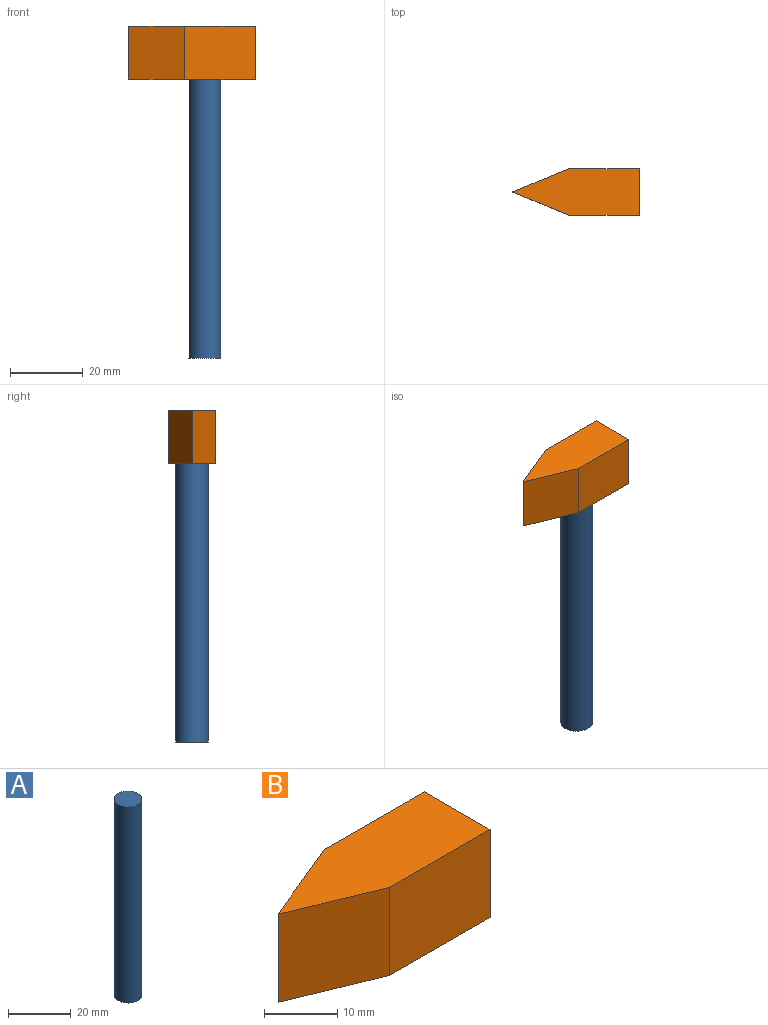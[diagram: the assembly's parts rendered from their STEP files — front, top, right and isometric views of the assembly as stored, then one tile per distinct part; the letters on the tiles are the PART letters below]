
ASSEMBLY  parts=2 mates=1
PART A: 3 faces, bbox 8.8x8.8x76.2 mm
  f0: plane 8.84x8.84mm, normal (0,0,1), area 61.4mm2, adj f2
  f1: plane 8.84x8.84mm, normal (0,0,-1), area 61.4mm2, adj f2
  f2: cylinder r=4.42mm len=76.2mm, axis (0,0,1), area 2115.9mm2, adj f0,f1
PART B: 7 faces, bbox 34.7x12.7x14.8 mm
  f0: plane 14.77x12.7mm, normal (1,0,0), area 187.5mm2, adj f1,f2,f3,f4
  f1: plane 34.72x12.7mm, normal (0,0,1), area 343.6mm2, adj f0,f3,f4,f5,f6
  f2: plane 34.72x12.7mm, normal (0,0,-1), area 343.6mm2, adj f0,f3,f4,f5,f6
  f3: plane 19.39x14.77mm, normal (0,-1,0), area 286.3mm2, adj f0,f1,f2,f5
  f4: plane 19.39x14.77mm, normal (0,1,0), area 286.3mm2, adj f0,f1,f2,f6
  f5: plane 15.33x14.77mm, normal (-0.38,-0.92,0), area 245mm2, adj f1,f2,f3,f6
  f6: plane 15.33x14.77mm, normal (-0.38,0.92,0), area 245mm2, adj f1,f2,f4,f5
PLACE A t=(52.75,17.93,29.26)mm
PLACE B t=(49.57,24.28,44.97)mm
MATE fastened A.f2 <-> B.f2  axis (0,0,1) through (40.7,17.93,60.66)mm
